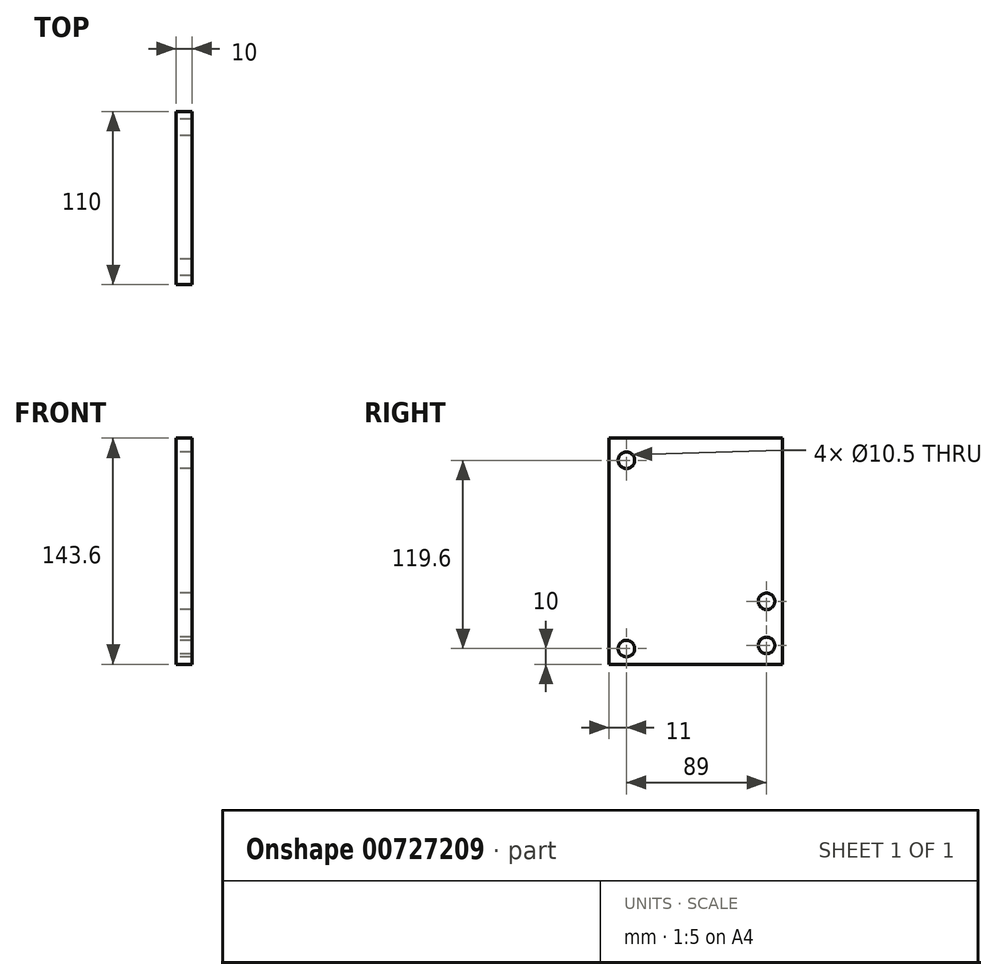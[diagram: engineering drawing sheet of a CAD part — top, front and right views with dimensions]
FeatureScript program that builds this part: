
annotation { "Feature Type Name" : "Feature", "Feature Type Description" : "" }
export const myFeature = defineFeature(function(context is Context, id is Id, definition is map)
    precondition{}
    {
        {
            var Q0;
            Q0=qCreatedBy(makeId("Right.planeOp"),FACE);
            var sketch = newSketch(context, id + "F0", { "sketchPlane" : qUnion([Q0])});
            skLineSegment(sketch, "E0.bottom", {"start": v(0, 0) * mm, "end": v(-110, 0) * mm});
            skLineSegment(sketch, "E0.top", {"start": v(0, 143.6) * mm, "end": v(-110, 143.6) * mm});
            skLineSegment(sketch, "E0.left", {"start": v(0, 0) * mm, "end": v(0, 143.6) * mm});
            skLineSegment(sketch, "E0.right", {"start": v(-110, 0) * mm, "end": v(-110, 143.6) * mm});
            skLineSegment(sketch, "E1", {"start": v(-10, 158.61) * mm, "end": v(-10, -19.83) * mm, "construction": true});
            skLineSegment(sketch, "E2", {"start": v(-129.81, 12) * mm, "end": v(4.19, 12) * mm, "construction": true});
            skLineSegment(sketch, "E3", {"start": v(-122.3, 10) * mm, "end": v(-85.51, 10) * mm, "construction": true});
            skLineSegment(sketch, "E4", {"start": v(-99, -15.26) * mm, "end": v(-99, 161) * mm, "construction": true});
            skPoint(sketch, "E5", {"position": v(-99, 10) * mm});
            skPoint(sketch, "E6", {"position": v(-10, 12) * mm});
            skLineSegment(sketch, "E7", {"start": v(-130.54, 40) * mm, "end": v(36.66, 40) * mm, "construction": true});
            skPoint(sketch, "E8", {"position": v(-10, 40) * mm});
            skLineSegment(sketch, "E9", {"start": v(-119.7, 129.6) * mm, "end": v(14.65, 129.6) * mm, "construction": true});
            skPoint(sketch, "E10", {"position": v(-99, 129.6) * mm});
            skCircle(sketch, "E11", {"center": v(-99, 129.6) * mm, "radius": 5.25 * mm});
            skCircle(sketch, "E12", {"center": v(-99, 10) * mm, "radius": 5.25 * mm});
            skCircle(sketch, "E13", {"center": v(-10, 12) * mm, "radius": 5.25 * mm});
            skCircle(sketch, "E14", {"center": v(-10, 40) * mm, "radius": 5.25 * mm});
            skSolve(sketch);
        }
        {
            var Q0;
            Q0=makeQuery(id+"F0.imprint","IMPRINT",FACE,{"disambiguationData":[TD([[makeQuery(id+"F0.imprint","IMPRINT",EDGE,{"derivedFrom":sQuery(id+"F0.wireOp",EDGE,"E0.bottom")}),-1.0]])]});
            extrude(context, id + "F1", {"entities" : qUnion([Q0]), "depth" : 10 * mm, "offsetDistance" : 25 * mm});
        }
    });
